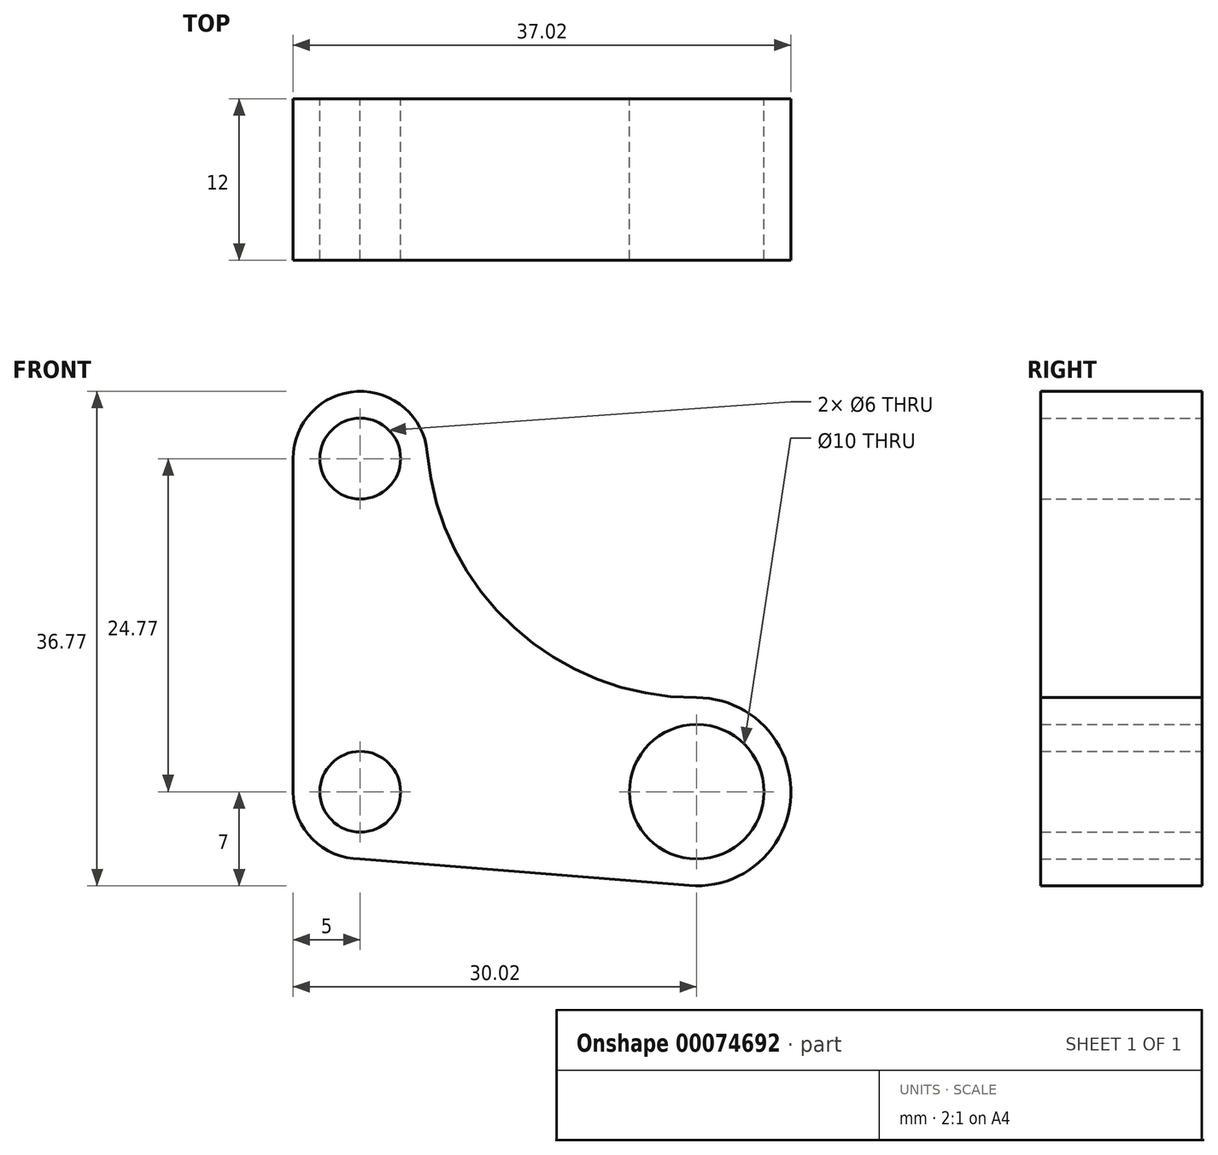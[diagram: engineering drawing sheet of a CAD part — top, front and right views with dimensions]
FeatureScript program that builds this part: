
annotation { "Feature Type Name" : "Feature", "Feature Type Description" : "" }
export const myFeature = defineFeature(function(context is Context, id is Id, definition is map)
    precondition{}
    {
        {
            var Q0;
            Q0=qCreatedBy(makeId("Front.planeOp"),FACE);
            var sketch = newSketch(context, id + "F0", { "sketchPlane" : qUnion([Q0])});
            skArc(sketch, "E0", {"start": v(-5, 0) * mm, "mid": v(-3.54, -3.54) * mm, "end": v(0, -5) * mm});
            skLineSegment(sketch, "E1", {"start": v(-5, 25.22) * mm, "end": v(-5, 0) * mm});
            skLineSegment(sketch, "E2", {"start": v(0, -5) * mm, "end": v(24.46, -6.98) * mm});
            skCircle(sketch, "E3", {"center": v(0, 24.77) * mm, "radius": 3 * mm});
            skCircle(sketch, "E4", {"center": v(0, 0) * mm, "radius": 3 * mm});
            skCircle(sketch, "E5", {"center": v(25.02, 0) * mm, "radius": 5 * mm});
            skArc(sketch, "E6", {"start": v(4.98, 25.22) * mm, "mid": v(-0.22, 29.77) * mm, "end": v(-5, 24.77) * mm});
            skArc(sketch, "E7", {"start": v(24.46, -6.98) * mm, "mid": v(32.01, -0.27) * mm, "end": v(24.99, 7) * mm});
            skArc(sketch, "E8", {"start": v(4.98, 25.22) * mm, "mid": v(11.44, 12.21) * mm, "end": v(24.99, 7) * mm});
            skSolve(sketch);
        }
        {
            var Q0;
            Q0=makeQuery(id+"F0.imprint","IMPRINT",FACE,{"disambiguationData":[TD([[makeQuery(id+"F0.imprint","IMPRINT",EDGE,{"derivedFrom":sQuery(id+"F0.wireOp",EDGE,"E0")}),1.0]])]});
            extrude(context, id + "F1", {"entities" : qUnion([Q0]), "depth" : 12 * mm});
        }
    });
